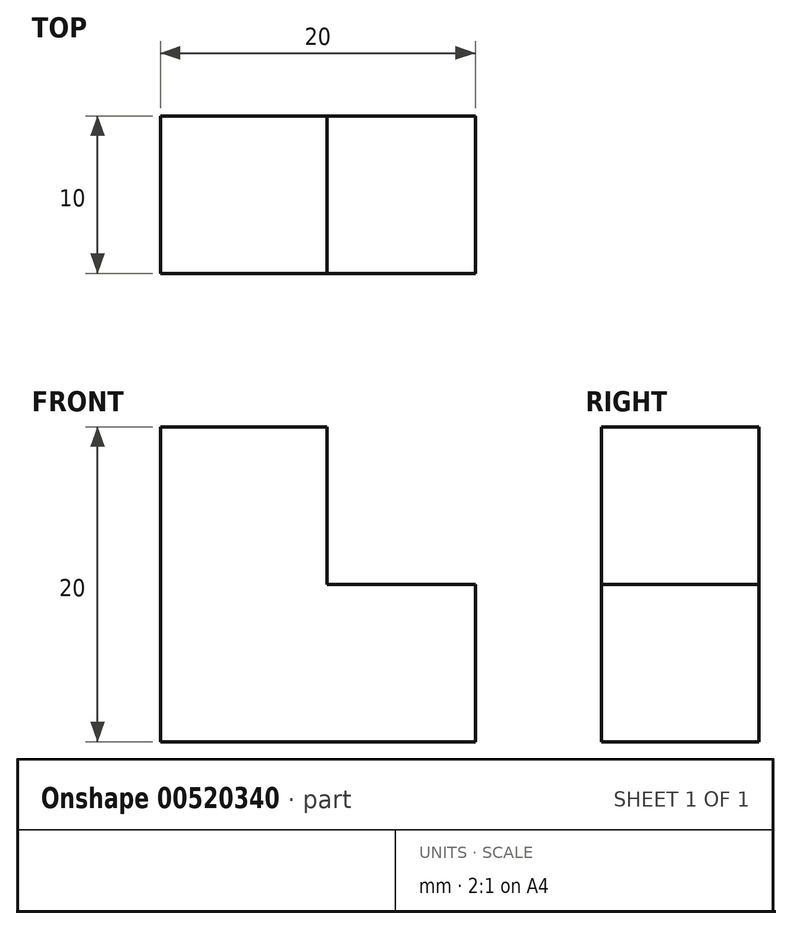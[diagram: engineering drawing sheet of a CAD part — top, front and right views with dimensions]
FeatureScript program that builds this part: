
annotation { "Feature Type Name" : "Feature", "Feature Type Description" : "" }
export const myFeature = defineFeature(function(context is Context, id is Id, definition is map)
    precondition{}
    {
        {
            var Q0;
            Q0=qCreatedBy(makeId("Front.planeOp"),FACE);
            var sketch = newSketch(context, id + "F0", { "sketchPlane" : qUnion([Q0])});
            skLineSegment(sketch, "E0", {"start": v(-65.54, 31.84) * mm, "end": v(-54.97, 31.84) * mm});
            skLineSegment(sketch, "E1", {"start": v(-54.97, 31.84) * mm, "end": v(-54.97, 21.84) * mm});
            skLineSegment(sketch, "E2", {"start": v(-54.97, 21.84) * mm, "end": v(-45.54, 21.84) * mm});
            skLineSegment(sketch, "E3", {"start": v(-45.54, 21.84) * mm, "end": v(-45.54, 11.84) * mm});
            skLineSegment(sketch, "E4", {"start": v(-45.54, 11.84) * mm, "end": v(-65.54, 11.84) * mm});
            skLineSegment(sketch, "E5", {"start": v(-65.54, 11.84) * mm, "end": v(-65.54, 31.84) * mm});
            skPoint(sketch, "E6.orphan", {"position": v(-64.97, 31.84) * mm});
            skSolve(sketch);
        }
        {
            var Q0;
            Q0=makeQuery(id+"F0.imprint","IMPRINT",FACE,{"disambiguationData":[TD([[makeQuery(id+"F0.imprint","IMPRINT",EDGE,{"derivedFrom":sQuery(id+"F0.wireOp",EDGE,"E0")}),-1.0]])]});
            extrude(context, id + "F1", {"entities" : qUnion([Q0]), "depth" : 10 * mm, "offsetDistance" : 25 * mm});
        }
    });
